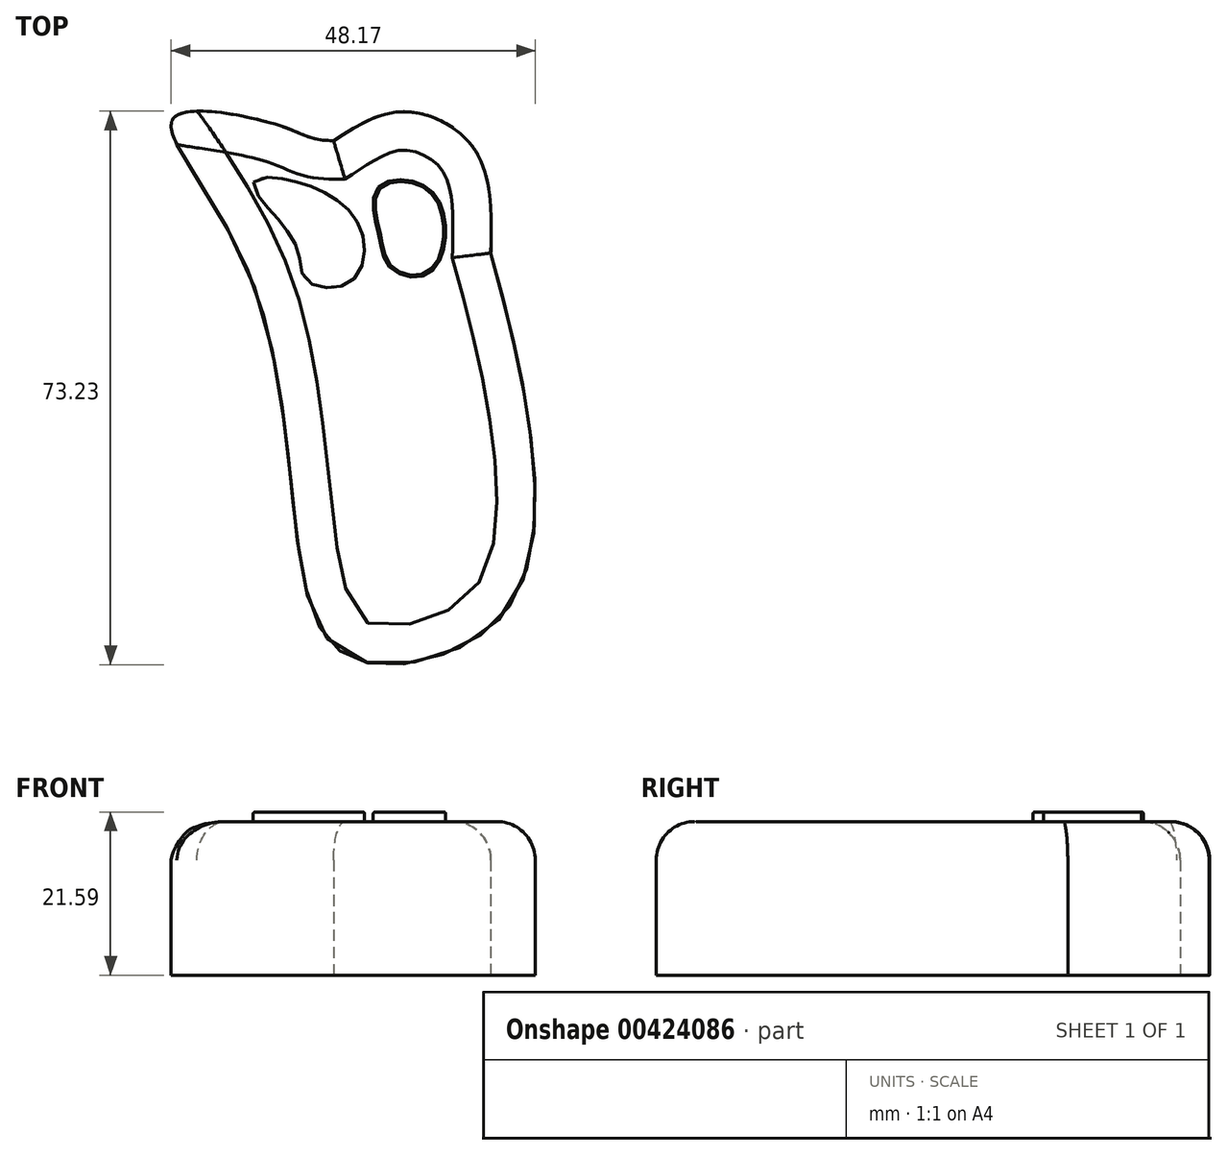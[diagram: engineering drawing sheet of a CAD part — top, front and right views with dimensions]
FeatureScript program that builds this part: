
annotation { "Feature Type Name" : "Feature", "Feature Type Description" : "" }
export const myFeature = defineFeature(function(context is Context, id is Id, definition is map)
    precondition{}
    {
        {
            var Q0;
            Q0=qCreatedBy(makeId("Top.planeOp"),FACE);
            var sketch = newSketch(context, id + "F0", { "sketchPlane" : qUnion([Q0])});
            skFitSpline(sketch, "E0", {"points": [v(-5.37, 15.26) * mm, v(-7.44, 28.84) * mm, v(-16.98, 33.96) * mm, v(-26.17, 30.13) * mm], "startDerivative": vector(0.96, 41.11) * mm, "endDerivative": vector(-27.98, -18.09) * mm});
            skFitSpline(sketch, "E1", {"points": [v(-26.17, 30.13) * mm, v(-32.64, 31.88) * mm, v(-47.22, 33.26) * mm, v(-37.45, 12.8) * mm, v(-29.3, -31.17) * mm, v(-20.93, -39.07) * mm, v(-3.72, -32.56) * mm, v(0, -9.77) * mm, v(-5.37, 15.26) * mm], "startDerivative": vector(-128.57, 0) * mm, "endDerivative": vector(-45.63, 166.9) * mm});
            skSolve(sketch);
        }
        {
            var Q0;
            Q0 = qSketchRegion(id + "F0", true);
            extrude(context, id + "F1", {"entities" : qUnion([Q0]), "depth" : 20.32 * mm});
        }
        {
            var Q0;
            Q0=makeQuery(id+"F1.opExtrude","CAP_FACE",FACE,{"disambiguationData":[OSD([sQuery(id+"F0.wireOp",EDGE,"E0"),sQuery(id+"F0.wireOp",EDGE,"E1")])],"isStart":false});
            fillet(context, id + "F2", {"entities" : qUnion([Q0]), "radius" : 5.08 * mm, "tangentPropagation" : true, "allowEdgeOverflow" : false});
        }
        {
            var Q0;
            Q0=qCreatedBy(makeId("Top.planeOp"),FACE);
            var sketch = newSketch(context, id + "F3", { "sketchPlane" : qUnion([Q0])});
            skFitSpline(sketch, "E2", {"points": [v(-36.75, 24.65) * mm, v(-31.4, 16.75) * mm, v(-29.77, 11.63) * mm, v(-23.72, 11.63) * mm, v(-24.42, 21.17) * mm, v(-36.75, 24.65) * mm]});
            skFitSpline(sketch, "E3", {"points": [v(-20.24, 23.96) * mm, v(-20.24, 17.68) * mm, v(-18.37, 13.02) * mm, v(-13.02, 13.02) * mm, v(-13.02, 23.26) * mm, v(-20.24, 23.96) * mm]});
            skSolve(sketch);
        }
        {
            var Q0;
            Q0 = qSketchRegion(id + "F3", true);
            extrude(context, id + "F4", {"entities" : qUnion([Q0]), "operationType" : NewBodyOperationType.ADD, "depth" : 21.59 * mm});
        }
        {
            var Q0;
            Q0=makeQuery(id+"F4.opExtrude","CAP_EDGE",EDGE,{"disambiguationData":[OSD([sQuery(id+"F3.wireOp",EDGE,"E3")])],"isStart":false});
            var Q1;
            Q1=makeQuery(id+"F4.opExtrude","CAP_EDGE",EDGE,{"disambiguationData":[OSD([sQuery(id+"F3.wireOp",EDGE,"E2")])],"isStart":false});
            fillet(context, id + "F5", {"entities" : qUnion([Q0, Q1]), "radius" : 0.25 * mm, "tangentPropagation" : true, "allowEdgeOverflow" : false});
        }
    });
